# Revit family: MaviGard gaz dedektörü
name_source: partatom
category: Fire Alarm Devices
units: mm (PartAtom-declared; Revit-internal decimal feet)

## family parameters
Cut with Voids When Loaded = No
Host = Face
Maintain Annotation Orientation = Yes
OmniClass Number = 23.85.30.21
OmniClass Title = Environmental Detection/Registration
Part Type = Normal
Room Calculation Point = No
Round Connector Dimension = Use Diameter
Shared = No

## types (13) — shared parameters
Code Performance = EN 50194-1
Color = Beyaz
Compatible sockets = ML-0120
Fax Number = (+)90 216 466 45 10
Installation Manual = https://mavilielektronik.com
Main Material = White Plastic PC/ABS
Manufacturer = Mavili Elektronik Ticaret A.Ş.
Model = MaviGard
Mounting surface = Duvara montaj
Nominal Depth = 50 mm
Nominal Height = 100 mm
Nominal Width = 140 mm
Operating temperature = (-10°C) - (+55°C)
Protection Sign = IP42
Secondary Material = Plastic
URL = https://www.mavili.com.tr
Warranty Duration Labor = 2
Warranty Duration Parts = 2
Warranty Duration Unit = Year
zero-valued in all types: Cost, Default Elevation

## per-type parameters (varying)
| type | Description | Device Adress Setup | External supply | Mounting height | Operating voltage range | Operatonal Voltage (default) | Product Code | Public Works Pose Number |
| MaviGard Karbonmonoksit gaz dedektörü 12 V 2 alarm seviyesi çıkışlı,elektrokimyasal | Karbonmonoksit gaz dedektörü [CO] |  | 24 V/DC | 150 cm | 12-33V/DC | 12 V/DC | GD2R-12EC | 833-610 |
| MaviGard Karbonmonoksit gaz dedektörü  24 V 2 alarm seviyesi çıkışlı,Elektrokimyasal | Karbonmonoksit gaz dedektörü [CO] |  | 24 V/DC | 150 cm | 18-33V/DC | 24 V/DC | GD2R-24EC | 833-610 |
| MaviGard Karbonmonoksit gaz dedektörü 220V AC 2 alarm seviyesi çıkışlı,Elektrokimyasal | Karbonmonoksit gaz dedektörü [CO] |  | 220 V/AC | 150 cm | 18-33V/DC | 24 V/DC | GD2R-220EC | 833-610 |
| MaviGard GDR serisi gaz dedektörleri LPG dedektörü, 12/24V DC, röle çıkışlı | LPG gaz dedektörü |  | 24 V/DC | 15-25 cm | 18-33V/DC | 24 V/DC | GDR-1224L | 833-606 |
| MaviGard GDR serisi gaz dedektörleri LPG  dedektörü, 220V AC, röle çıkışlı | LPG gaz dedektörü |  | 220 V/DC | 15-25 cm | 18-33V/DC | 24 V/DC | GDR-220L | 833-606 |
| MaviGard GDR serisi gaz dedektörleri metan dedektörü, 12/24V DC, röle çıkışlı | Metan gaz dedektörü |  | 24 V/DC | Tavandan 5-15 cm aşağıda | 12-33V/DC | 24 V/DC | GDR-1224M | 833-608 |
| MaviGard GDR serisi gaz dedektörleri metan dedektörü 220 V AC , röle çıkışlı | Metan gaz dedektörü |  | 220 V/AC | Tavandan 5-15 cm aşağıda | 18-33V/DC | 24 V/DC | GDR-220M | 833-608 |
| MaviGard AGD serisi gaz dedektörleri akıllı adresli  karbonmonoksit dedektörü,12/24V DC | Akıllı adresli karbonmonoksit gaz dedektörü | El tipi adresleme cihazı | 24 V/DC | 150 cm | 12-33V/DC | 24 V/DC | AGD-1224EC.VIP |  |
| MaviGard AGD serisi gaz dedektörleri akıllı adresli karbonmonoksit dedektörü,220V AC | Akıllı adresli karbonmonoksit gaz dedektörü | El tipi adresleme cihazı | 220 V/AC | 150 cm | 12-33V/DC | 24 V/DC | AGD-220EC.VIP |  |
| MaviGard AGD serisi gaz dedektörleri akıllı adresli LPG dedektörü,12/24V DC | Akıllı adresli LPG gaz dedektörü | El tipi adresleme cihazı | 24 V/DC | 15-25 cm | 12-33V/DC | 24 V/DC | AGD-1224L.VIP | 833-605 |
| MaviGard AGD serisi gaz dedektörleri akıllı adresli LPG dedektörü,220V AC | Akıllı adresli LPG gaz dedektörü | El tipi adresleme cihazı | 220 V/AC | 15-25 cm | 12-33V/DC | 24 V/DC | AGD-220L.VIP |  |
| MaviGard AGD serisi gaz dedektörleri akıllı adresli metan dedektörü,12/24V DC | Akıllı adresli Metan gaz dedektörü | El tipi adresleme cihazı | 24 V/DC | Tavandan 5-15 cm aşağıda | 12-33V/DC | 24 V/DC | AGD-1224M.VIP | 833-607 |
| MaviGard AGD serisi gaz dedektörleri akıllı adresli metan dedektörü,220V AC | Akıllı adresli Metan gaz dedektörü | El tipi adresleme cihazı | 220 V/AC | Tavandan 5-15 cm aşağıda | 12-33V/DC | 24 V/DC | AGD-220M.VIP |  |

## geometry (parser evidence)
native form markers: Sweep x1
no freeform markers — native parametric forms only
